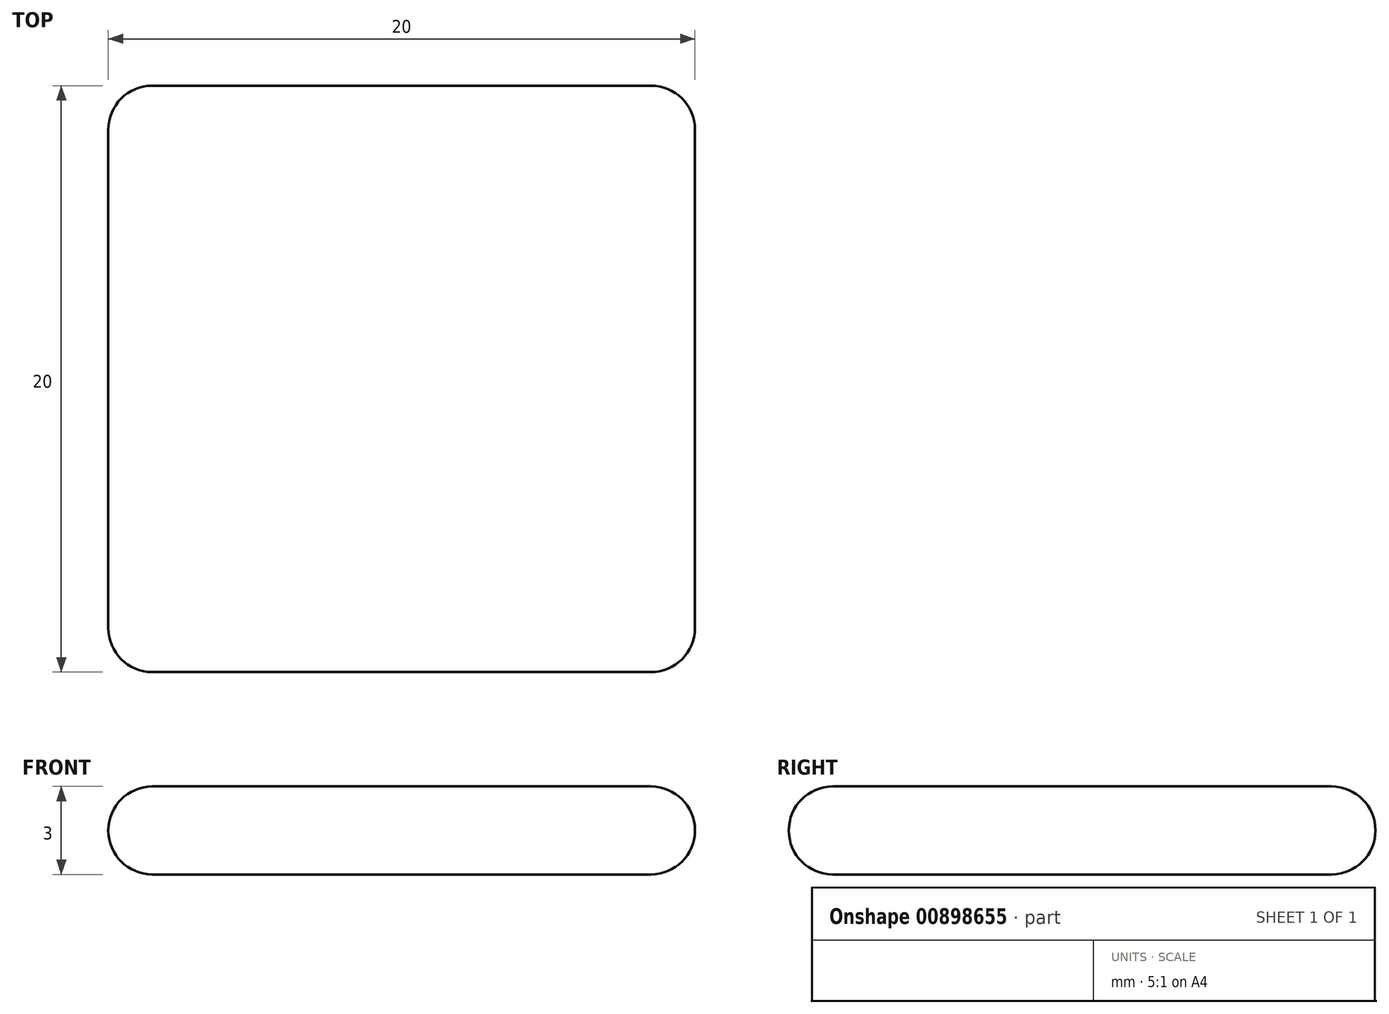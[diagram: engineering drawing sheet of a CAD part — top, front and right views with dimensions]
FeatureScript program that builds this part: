
annotation { "Feature Type Name" : "Feature", "Feature Type Description" : "" }
export const myFeature = defineFeature(function(context is Context, id is Id, definition is map)
    precondition{}
    {
        {
            var Q0;
            Q0=qCreatedBy(makeId("Top.planeOp"),FACE);
            var sketch = newSketch(context, id + "F0", { "sketchPlane" : qUnion([Q0])});
            skLineSegment(sketch, "E0.bottom", {"start": v(-20, 20) * mm, "end": v(0, 20) * mm});
            skLineSegment(sketch, "E0.top", {"start": v(-20, 0) * mm, "end": v(0, 0) * mm});
            skLineSegment(sketch, "E0.left", {"start": v(-20, 20) * mm, "end": v(-20, 0) * mm});
            skLineSegment(sketch, "E0.right", {"start": v(0, 20) * mm, "end": v(0, 0) * mm});
            skSolve(sketch);
        }
        {
            var Q0;
            Q0=makeQuery(id+"F0.imprint","IMPRINT",FACE,{"disambiguationData":[TD([[makeQuery(id+"F0.imprint","IMPRINT",EDGE,{"derivedFrom":sQuery(id+"F0.wireOp",EDGE,"E0.bottom")}),-1.0]])]});
            extrude(context, id + "F1", {"entities" : qUnion([Q0]), "depth" : 3 * mm, "offsetDistance" : 25 * mm});
        }
        {
            var Q0;
            Q0=makeQuery(id+"F1.opExtrude","CAP_FACE",FACE,{"disambiguationData":[OSD([sQuery(id+"F0.wireOp",EDGE,"E0.bottom"),sQuery(id+"F0.wireOp",EDGE,"E0.top"),sQuery(id+"F0.wireOp",EDGE,"E0.left"),sQuery(id+"F0.wireOp",EDGE,"E0.right")])],"isStart":false});
            var Q1;
            Q1=makeQuery(id+"F1.opExtrude","CAP_FACE",FACE,{"disambiguationData":[OSD([sQuery(id+"F0.wireOp",EDGE,"E0.bottom"),sQuery(id+"F0.wireOp",EDGE,"E0.top"),sQuery(id+"F0.wireOp",EDGE,"E0.left"),sQuery(id+"F0.wireOp",EDGE,"E0.right")])],"isStart":true});
            var Q2;
            Q2=makeQuery(id+"F1.opExtrude","SWEPT_EDGE",EDGE,{"disambiguationData":[OSD([sQuery(id+"F0.wireOp",EDGE,"E0.top"),sQuery(id+"F0.wireOp",EDGE,"E0.left")])]});
            var Q3;
            Q3=makeQuery(id+"F1.opExtrude","SWEPT_EDGE",EDGE,{"disambiguationData":[OSD([sQuery(id+"F0.wireOp",EDGE,"E0.top"),sQuery(id+"F0.wireOp",EDGE,"E0.right")])]});
            var Q4;
            Q4=makeQuery(id+"F1.opExtrude","SWEPT_EDGE",EDGE,{"disambiguationData":[OSD([sQuery(id+"F0.wireOp",EDGE,"E0.bottom"),sQuery(id+"F0.wireOp",EDGE,"E0.left")])]});
            var Q5;
            Q5=makeQuery(id+"F1.opExtrude","SWEPT_EDGE",EDGE,{"disambiguationData":[OSD([sQuery(id+"F0.wireOp",EDGE,"E0.bottom"),sQuery(id+"F0.wireOp",EDGE,"E0.right")])]});
            fillet(context, id + "F2", {"entities" : qUnion([Q0, Q1, Q2, Q3, Q4, Q5]), "radius" : 1.5 * mm, "tangentPropagation" : true, "allowEdgeOverflow" : false});
        }
    });
